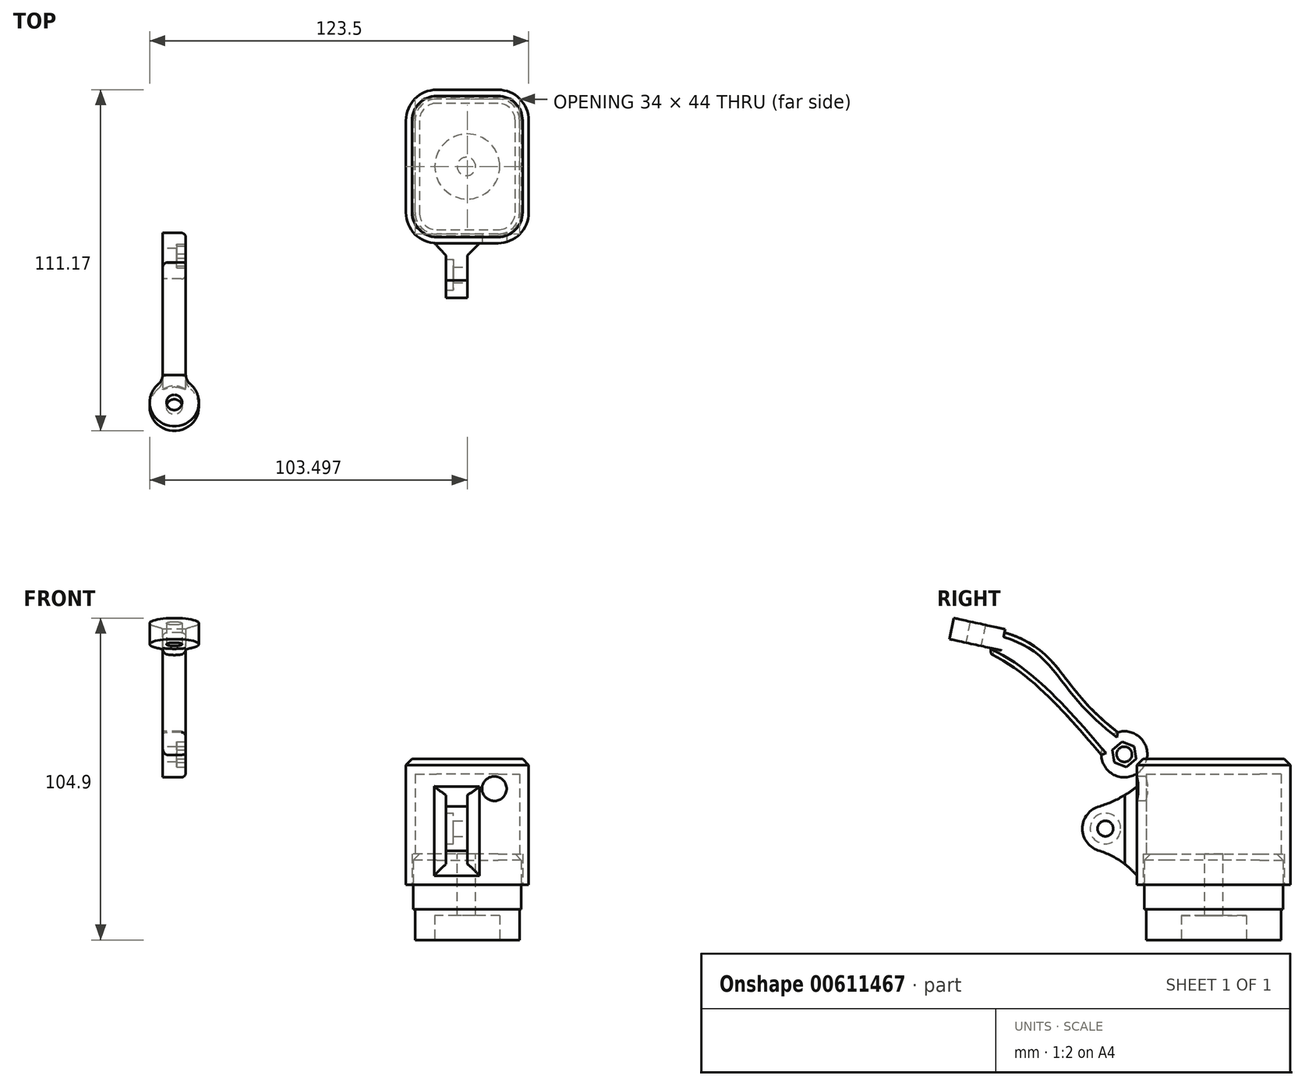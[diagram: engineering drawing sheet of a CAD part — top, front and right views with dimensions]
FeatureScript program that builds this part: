
annotation { "Feature Type Name" : "Feature", "Feature Type Description" : "" }
export const myFeature = defineFeature(function(context is Context, id is Id, definition is map)
    precondition{}
    {
        {
            var Q0;
            Q0=qCreatedBy(makeId("Right.planeOp"),FACE);
            var sketch = newSketch(context, id + "F0", { "sketchPlane" : qUnion([Q0])});
            skCircle(sketch, "E0", {"center": v(-29.14, 42.5) * mm, "radius": 3.6 * mm});
            skCircle(sketch, "E1", {"center": v(-29.14, 42.5) * mm, "radius": 5 * mm});
            skLineSegment(sketch, "E2", {"start": v(-69.14, 82.5) * mm, "end": v(-82.83, 85.47) * mm});
            skCircle(sketch, "E3", {"center": v(-29.14, 42.5) * mm, "radius": 7.5 * mm});
            skFitSpline(sketch, "E4", {"points": [v(-11.21, 52.43) * mm, v(-17.95, 9.37) * mm], "startDerivative": vector(-15.47, -15.75) * mm, "endDerivative": vector(-1.67, -37.36) * mm});
            skFitSpline(sketch, "E5", {"points": [v(-22.8, 46.5) * mm, v(-11.21, 52.43) * mm], "startDerivative": vector(15.63, -7.91) * mm, "endDerivative": vector(13.09, 9.04) * mm});
            skFitSpline(sketch, "E6", {"points": [v(-32.57, 35.83) * mm, v(-17.95, 9.37) * mm], "startDerivative": vector(25.66, -14.01) * mm, "endDerivative": vector(10.19, -17.27) * mm});
            skLineSegment(sketch, "E7", {"start": v(-16.89, 47.19) * mm, "end": v(-26.36, 29.28) * mm});
            skLineSegment(sketch, "E8.0", {"start": v(-69.4, 76.41) * mm, "end": v(-84.58, 79.7) * mm});
            skLineSegment(sketch, "E9", {"start": v(-69.4, 76.41) * mm, "end": v(-69.14, 82.5) * mm});
            skLineSegment(sketch, "E10", {"start": v(-84.58, 79.7) * mm, "end": v(-82.83, 85.47) * mm});
            skCircle(sketch, "E11", {"center": v(-29.14, 42.5) * mm, "radius": 6.25 * mm});
            skFitSpline(sketch, "E12", {"points": [v(-35.04, 40.42) * mm, v(-84.58, 79.7) * mm], "startDerivative": vector(-65.8, 78.38) * mm, "endDerivative": vector(-54.37, 15.9) * mm});
            skFitSpline(sketch, "E13", {"points": [v(-28.15, 47.4) * mm, v(-69.14, 82.5) * mm], "startDerivative": vector(-71.86, 50.82) * mm, "endDerivative": vector(-64.05, 18.36) * mm});
            skCircle(sketch, "E14.cCircle", {"center": v(-29.14, 42.5) * mm, "radius": 3.6 * mm, "construction": true});
            skLineSegment(sketch, "E14.0", {"start": v(-33.03, 43.97) * mm, "end": v(-29.82, 46.6) * mm});
            skLineSegment(sketch, "E14.1", {"start": v(-29.82, 46.6) * mm, "end": v(-25.93, 45.13) * mm});
            skLineSegment(sketch, "E14.2", {"start": v(-25.93, 45.13) * mm, "end": v(-25.26, 41.03) * mm});
            skLineSegment(sketch, "E14.3", {"start": v(-25.26, 41.03) * mm, "end": v(-28.47, 38.4) * mm});
            skLineSegment(sketch, "E14.4", {"start": v(-28.47, 38.4) * mm, "end": v(-32.36, 39.87) * mm});
            skLineSegment(sketch, "E14.5", {"start": v(-32.36, 39.87) * mm, "end": v(-33.03, 43.97) * mm});
            skPoint(sketch, "E14.0.midPoint", {"position": v(-31.42, 45.28) * mm});
            skSolve(sketch);
        }
        {
            var Q0;
            {var subQ1=sQuery(id+"F0.wireOp",EDGE,"E8.0");Q0=makeQuery(id+"F0.imprint","IMPRINT",FACE,{"disambiguationData":[TD([[makeQuery(id+"F0.imprint","IMPRINT",EDGE,{"derivedFrom":subQ1}),1.0]])]});}
            var Q1;
            {var subQ0=sQuery(id+"F0.wireOp",EDGE,"E13");var subQ1=sQuery(id+"F0.wireOp",EDGE,"E3");var subQ2=makeQuery(id+"F0.imprint","INTERSECT",VERTEX,{"derivedFrom":[subQ1,subQ0]});Q1=makeQuery(id+"F0.imprint","IMPRINT",FACE,{"disambiguationData":[TD([[makeQuery(id+"F0.imprint","IMPRINT",EDGE,{"disambiguationData":[TD([[subQ2,-1.0]])],"derivedFrom":subQ1}),1.0]])]});}
            var Q2;
            Q2=makeQuery(id+"F0.imprint","IMPRINT",FACE,{"disambiguationData":[TD([[makeQuery(id+"F0.imprint","IMPRINT",EDGE,{"derivedFrom":sQuery(id+"F0.wireOp",EDGE,"E1")}),-1.0]])]});
            var Q3;
            Q3=makeQuery(id+"F0.imprint","IMPRINT",FACE,{"disambiguationData":[TD([[makeQuery(id+"F0.imprint","IMPRINT",EDGE,{"derivedFrom":sQuery(id+"F0.wireOp",EDGE,"E0")}),-1.0]])]});
            var Q4;
            Q4=makeQuery(id+"F0.imprint","IMPRINT",FACE,{"disambiguationData":[TD([[makeQuery(id+"F0.imprint","IMPRINT",EDGE,{"derivedFrom":sQuery(id+"F0.wireOp",EDGE,"E0")}),1.0]])]});
            var Q5;
            Q5=makeQuery(id+"F0.imprint","IMPRINT",FACE,{"disambiguationData":[TD([[makeQuery(id+"F0.imprint","IMPRINT",EDGE,{"derivedFrom":sQuery(id+"F0.wireOp",EDGE,"E1")}),1.0]])]});
            var Q6;
            {var subQ1=sQuery(id+"F0.wireOp",EDGE,"E3");var subQ4=makeQuery(id+"F0.imprint","INTERSECT",VERTEX,{"derivedFrom":[subQ1,sQuery(id+"F0.wireOp",EDGE,"E5")]});Q6=makeQuery(id+"F0.imprint","IMPRINT",FACE,{"disambiguationData":[TD([[makeQuery(id+"F0.imprint","IMPRINT",EDGE,{"disambiguationData":[TD([[subQ4,-1.0]])],"derivedFrom":subQ1}),1.0]])]});}
            extrude(context, id + "F1", {"entities" : qUnion([Q0, Q1, Q2, Q3, Q4, Q5, Q6]), "depth" : 7.5 * mm, "offsetDistance" : 25 * mm});
        }
        {
            var Q0;
            Q0=makeQuery(id+"F1.opExtrude","CAP_FACE",FACE,{"disambiguationData":[OSD([sQuery(id+"F0.wireOp",EDGE,"E8.0"),sQuery(id+"F0.wireOp",EDGE,"E9"),sQuery(id+"F0.wireOp",EDGE,"E11"),sQuery(id+"F0.wireOp",EDGE,"E12"),sQuery(id+"F0.wireOp",EDGE,"E13")])],"isStart":false});
            var sketch = newSketch(context, id + "F2", { "sketchPlane" : qUnion([Q0])});
            skLineSegment(sketch, "E15.0", {"start": v(-32.36, 39.87) * mm, "end": v(-33.03, 43.97) * mm});
            skLineSegment(sketch, "E15.1", {"start": v(-28.47, 38.4) * mm, "end": v(-32.36, 39.87) * mm});
            skLineSegment(sketch, "E15.2", {"start": v(-25.26, 41.03) * mm, "end": v(-28.47, 38.4) * mm});
            skLineSegment(sketch, "E15.3", {"start": v(-25.93, 45.13) * mm, "end": v(-25.26, 41.03) * mm});
            skLineSegment(sketch, "E15.4", {"start": v(-29.82, 46.6) * mm, "end": v(-25.93, 45.13) * mm});
            skLineSegment(sketch, "E15.5", {"start": v(-33.03, 43.97) * mm, "end": v(-29.82, 46.6) * mm});
            skSolve(sketch);
        }
        {
            var Q0;
            Q0=makeQuery(id+"F2.imprint","IMPRINT",FACE,{"disambiguationData":[TD([[makeQuery(id+"F2.imprint","IMPRINT",EDGE,{"derivedFrom":sQuery(id+"F2.wireOp",EDGE,"E15.0")}),-1.0]])]});
            extrude(context, id + "F3", {"entities" : qUnion([Q0]), "operationType" : NewBodyOperationType.REMOVE, "oppositeDirection" : true, "depth" : 3 * mm});
        }
        {
            var Q0;
            Q0=sQuery(id+"F0.wireOp",VERTEX,"E0.center");
            var Q1;
            Q1=makeQuery(id+"F1.opExtrude","SWEPT_BODY",BODY,{"disambiguationData":[OSD([sQuery(id+"F0.wireOp",EDGE,"E3"),sQuery(id+"F0.wireOp",EDGE,"E6"),sQuery(id+"F0.wireOp",EDGE,"E8.0"),sQuery(id+"F0.wireOp",EDGE,"E9"),sQuery(id+"F0.wireOp",EDGE,"E12"),sQuery(id+"F0.wireOp",EDGE,"E13")])]});
            hole(context, id + "F4", {"style" : HoleStyle.SIMPLE, "endStyle" : HoleEndStyle.THROUGH, "oppositeDirection" : true, "holeDiameter" : 5 * mm, "isTappedThrough" : true, "tappedDepth" : 12 * mm, "tapClearance" : 3, "locations" : qUnion([Q0]), "scope" : qUnion([Q1]), "majorDiameter" : 5 * mm});
        }
        {
            var Q0;
            Q0=makeQuery(id+"F1.opExtrude","CAP_EDGE",EDGE,{"disambiguationData":[OSD([sQuery(id+"F0.wireOp",EDGE,"E12")])],"isStart":false});
            var Q1;
            Q1=makeQuery(id+"F1.opExtrude","CAP_EDGE",EDGE,{"disambiguationData":[OSD([sQuery(id+"F0.wireOp",EDGE,"E13")])],"isStart":false});
            var Q2;
            Q2=makeQuery(id+"F1.opExtrude","CAP_EDGE",EDGE,{"disambiguationData":[OSD([sQuery(id+"F0.wireOp",EDGE,"E12")])],"isStart":true});
            var Q3;
            Q3=makeQuery(id+"F1.opExtrude","CAP_EDGE",EDGE,{"disambiguationData":[OSD([sQuery(id+"F0.wireOp",EDGE,"E13")])],"isStart":true});
            var Q4;
            {var subQ0=sQuery(id+"F0.wireOp",EDGE,"E3");var subQ1=makeQuery(id+"F0.imprint","INTERSECT",VERTEX,{"derivedFrom":[subQ0,sQuery(id+"F0.wireOp",EDGE,"E5")]});Q4=makeQuery(id+"F1.opExtrude","CAP_EDGE",EDGE,{"disambiguationData":[OSD([subQ0]),TDD([makeQuery(id+"F0.imprint","IMPRINT",EDGE,{"disambiguationData":[TD([[subQ1,-1.0]])],"derivedFrom":subQ0}),makeQuery(id+"F0.imprint","IMPRINT",EDGE,{"disambiguationData":[TD([[subQ1,1.0]])],"derivedFrom":subQ0})])],"isStart":false});}
            var Q5;
            Q5=makeQuery(id+"F1.opExtrude","CAP_EDGE",EDGE,{"disambiguationData":[OSD([sQuery(id+"F0.wireOp",EDGE,"E6")])],"isStart":false});
            var Q6;
            {var subQ0=sQuery(id+"F0.wireOp",EDGE,"E3");Q6=makeQuery(id+"F1.opExtrude","CAP_EDGE",EDGE,{"disambiguationData":[OSD([subQ0]),TDD([makeQuery(id+"F0.imprint","IMPRINT",EDGE,{"disambiguationData":[TD([[makeQuery(id+"F0.imprint","INTERSECT",VERTEX,{"disambiguationData":[OD(0.0)],"derivedFrom":[subQ0,sQuery(id+"F0.wireOp",EDGE,"E6")]}),1.0]])],"derivedFrom":subQ0})])],"isStart":false});}
            fillet(context, id + "F5", {"entities" : qUnion([Q0, Q1, Q2, Q3, Q4, Q5, Q6]), "radius" : 1.5 * mm, "tangentPropagation" : true, "allowEdgeOverflow" : false});
        }
        {
            var Q0;
            Q0=makeQuery(id+"F1.opExtrude","SWEPT_FACE",FACE,{"disambiguationData":[OSD([sQuery(id+"F0.wireOp",EDGE,"E8.0")])]});
            var sketch = newSketch(context, id + "F6", { "sketchPlane" : qUnion([Q0])});
            skCircle(sketch, "E16", {"center": v(3.75, -93.2) * mm, "radius": 8 * mm});
            skPoint(sketch, "E16.centerSnap0", {"position": v(3.75, -99.56) * mm});
            skSolve(sketch);
        }
        {
            var Q0;
            {var subQ0=sQuery(id+"F0.wireOp",EDGE,"E8.0");var subQ1=makeQuery(id+"F1.opExtrude","SWEPT_FACE",FACE,{"disambiguationData":[OSD([subQ0])]});var subQ2=sQuery(id+"F0.wireOp",EDGE,"E12");var subQ4=makeQuery(id+"F5.opFillet","BLEND_EDGE",EDGE,{"blendedFrom":[makeQuery(id+"F1.opExtrude","CAP_EDGE",EDGE,{"disambiguationData":[OSD([subQ2])],"isStart":true}),subQ1],"blendedInto":[subQ1]});Q0=makeQuery(id+"F6.imprint","IMPRINT",FACE,{"disambiguationData":[TD([[makeQuery(id+"F6.imprint","IMPRINT",EDGE,{"derivedFrom":subQ4}),-1.0]])]});}
            var Q1;
            {var subQ0=sQuery(id+"F0.wireOp",EDGE,"E8.0");var subQ1=makeQuery(id+"F1.opExtrude","SWEPT_FACE",FACE,{"disambiguationData":[OSD([subQ0])]});var subQ2=sQuery(id+"F0.wireOp",EDGE,"E12");var subQ3=makeQuery(id+"F5.opFillet","BLEND_EDGE",EDGE,{"blendedFrom":[makeQuery(id+"F1.opExtrude","CAP_EDGE",EDGE,{"disambiguationData":[OSD([subQ2])],"isStart":true}),subQ1],"blendedInto":[subQ1]});Q1=makeQuery(id+"F6.imprint","IMPRINT",FACE,{"disambiguationData":[TD([[makeQuery(id+"F6.imprint","IMPRINT",EDGE,{"derivedFrom":subQ3}),1.0]])]});}
            var Q2;
            {var subQ1=sQuery(id+"F0.wireOp",EDGE,"E8.0");var subQ6=makeQuery(id+"F1.opExtrude","SWEPT_EDGE",EDGE,{"disambiguationData":[OSD([subQ1,sQuery(id+"F0.wireOp",EDGE,"E9")])]});Q2=makeQuery(id+"F6.imprint","IMPRINT",FACE,{"disambiguationData":[TD([[makeQuery(id+"F6.imprint","IMPRINT",EDGE,{"derivedFrom":subQ6}),1.0]])]});}
            extrude(context, id + "F7", {"entities" : qUnion([Q0, Q1, Q2]), "operationType" : NewBodyOperationType.ADD, "depth" : 7 * mm, "offsetDistance" : 25 * mm});
        }
        {
            var Q0;
            Q0=sQuery(id+"F6.wireOp",VERTEX,"E16.center");
            var Q1;
            Q1=makeQuery(id+"F1.opExtrude","SWEPT_BODY",BODY,{"disambiguationData":[OSD([sQuery(id+"F0.wireOp",EDGE,"E3"),sQuery(id+"F0.wireOp",EDGE,"E6"),sQuery(id+"F0.wireOp",EDGE,"E8.0"),sQuery(id+"F0.wireOp",EDGE,"E9"),sQuery(id+"F0.wireOp",EDGE,"E12"),sQuery(id+"F0.wireOp",EDGE,"E13")])]});
            hole(context, id + "F8", {"style" : HoleStyle.SIMPLE, "endStyle" : HoleEndStyle.THROUGH, "oppositeDirection" : true, "holeDiameter" : 5.1 * mm, "isTappedThrough" : true, "tappedDepth" : 12 * mm, "tapClearance" : 3, "locations" : qUnion([Q0]), "scope" : qUnion([Q1]), "majorDiameter" : 5 * mm});
        }
        {
            var Q0;
            Q0=sQuery(id+"F6.wireOp",VERTEX,"E16.center");
            var Q1;
            Q1=makeQuery(id+"F1.opExtrude","SWEPT_BODY",BODY,{"disambiguationData":[OSD([sQuery(id+"F0.wireOp",EDGE,"E3"),sQuery(id+"F0.wireOp",EDGE,"E6"),sQuery(id+"F0.wireOp",EDGE,"E8.0"),sQuery(id+"F0.wireOp",EDGE,"E9"),sQuery(id+"F0.wireOp",EDGE,"E12"),sQuery(id+"F0.wireOp",EDGE,"E13")])]});
            hole(context, id + "F9", {"style" : HoleStyle.C_BORE, "endStyle" : HoleEndStyle.THROUGH, "holeDiameter" : 5 * mm, "cBoreDiameter" : 14 * mm, "cBoreDepth" : 4 * mm, "isTappedThrough" : true, "tappedDepth" : 12 * mm, "tapClearance" : 3, "locations" : qUnion([Q0]), "scope" : qUnion([Q1]), "majorDiameter" : 5 * mm});
        }
        {
            var Q0;
            {var subQ0=sQuery(id+"F6.wireOp",EDGE,"E16");var subQ1=sQuery(id+"F0.wireOp",EDGE,"E8.0");Q0=makeQuery(id+"F7.opExtrude","SWEPT_EDGE",EDGE,{"disambiguationData":[OSD([subQ1,subQ0]),TDD([makeQuery(id+"F6.imprint","INTERSECT",VERTEX,{"derivedFrom":[makeQuery(id+"F1.opExtrude","CAP_EDGE",EDGE,{"disambiguationData":[OSD([subQ1])],"isStart":false}),subQ0]})])]});}
            var Q1;
            {var subQ0=sQuery(id+"F6.wireOp",EDGE,"E16");var subQ1=sQuery(id+"F0.wireOp",EDGE,"E8.0");Q1=makeQuery(id+"F7.opExtrude","SWEPT_EDGE",EDGE,{"disambiguationData":[OSD([subQ1,subQ0]),TDD([makeQuery(id+"F6.imprint","INTERSECT",VERTEX,{"derivedFrom":[makeQuery(id+"F1.opExtrude","CAP_EDGE",EDGE,{"disambiguationData":[OSD([subQ1])],"isStart":true}),subQ0]})])]});}
            fillet(context, id + "F10", {"entities" : qUnion([Q0, Q1]), "radius" : 4.6 * mm, "tangentPropagation" : true, "allowEdgeOverflow" : false});
        }
        {
            var Q0;
            Q0=qCreatedBy(makeId("Top.planeOp"),FACE);
            var sketch = newSketch(context, id + "F11", { "sketchPlane" : qUnion([Q0])});
            skLineSegment(sketch, "E17.bottom", {"start": v(109.25, -25) * mm, "end": v(89.25, -25) * mm});
            skLineSegment(sketch, "E17.top", {"start": v(109.25, 25) * mm, "end": v(89.25, 25) * mm});
            skLineSegment(sketch, "E17.left", {"start": v(119.25, -15) * mm, "end": v(119.25, 15) * mm});
            skLineSegment(sketch, "E17.right", {"start": v(79.25, -15) * mm, "end": v(79.25, 15) * mm});
            skPoint(sketch, "E17.middle", {"position": v(99.25, 0) * mm});
            skPoint(sketch, "E18.visualSharp", {"position": v(79.25, -25) * mm});
            skArc(sketch, "E18.filletArc", {"start": v(79.25, -15) * mm, "mid": v(82.18, -22.07) * mm, "end": v(89.25, -25) * mm});
            skPoint(sketch, "E19.visualSharp", {"position": v(119.25, -25) * mm});
            skArc(sketch, "E19.filletArc", {"start": v(109.25, -25) * mm, "mid": v(116.32, -22.07) * mm, "end": v(119.25, -15) * mm});
            skPoint(sketch, "E20.visualSharp", {"position": v(119.25, 25) * mm});
            skArc(sketch, "E20.filletArc", {"start": v(119.25, 15) * mm, "mid": v(116.32, 22.07) * mm, "end": v(109.25, 25) * mm});
            skPoint(sketch, "E21.visualSharp", {"position": v(79.25, 25) * mm});
            skArc(sketch, "E21.filletArc", {"start": v(89.25, 25) * mm, "mid": v(82.18, 22.07) * mm, "end": v(79.25, 15) * mm});
            skLineSegment(sketch, "E22.0", {"start": v(117.25, -15) * mm, "end": v(117.25, 15) * mm});
            skArc(sketch, "E22.1", {"start": v(109.25, -23) * mm, "mid": v(114.9, -20.66) * mm, "end": v(117.25, -15) * mm});
            skArc(sketch, "E22.2", {"start": v(117.25, 15) * mm, "mid": v(114.9, 20.66) * mm, "end": v(109.25, 23) * mm});
            skLineSegment(sketch, "E22.3", {"start": v(109.25, -23) * mm, "end": v(89.25, -23) * mm});
            skLineSegment(sketch, "E22.4", {"start": v(109.25, 23) * mm, "end": v(89.25, 23) * mm});
            skArc(sketch, "E22.5", {"start": v(89.25, 23) * mm, "mid": v(83.6, 20.66) * mm, "end": v(81.25, 15) * mm});
            skLineSegment(sketch, "E22.6", {"start": v(81.25, -15) * mm, "end": v(81.25, 15) * mm});
            skArc(sketch, "E22.7", {"start": v(81.25, -15) * mm, "mid": v(83.6, -20.66) * mm, "end": v(89.25, -23) * mm});
            skLineSegment(sketch, "E23", {"start": v(99.25, 34.03) * mm, "end": v(99.25, -73.15) * mm, "construction": true});
            skPoint(sketch, "E23.endSnap0", {"position": v(99.25, -25) * mm});
            skPoint(sketch, "E24.visualSharp", {"position": v(111.25, 7) * mm});
            skPoint(sketch, "E25.visualSharp", {"position": v(87.25, 7) * mm});
            skPoint(sketch, "E26.visualSharp", {"position": v(87.25, -7) * mm});
            skPoint(sketch, "E27.visualSharp", {"position": v(111.25, -7) * mm});
            skArc(sketch, "E28.0", {"start": v(109.25, -22) * mm, "mid": v(114.2, -19.95) * mm, "end": v(116.25, -15) * mm});
            skLineSegment(sketch, "E28.1", {"start": v(109.25, -22) * mm, "end": v(89.25, -22) * mm});
            skLineSegment(sketch, "E28.2", {"start": v(116.25, -15) * mm, "end": v(116.25, 15) * mm});
            skArc(sketch, "E28.3", {"start": v(82.25, -15) * mm, "mid": v(84.3, -19.95) * mm, "end": v(89.25, -22) * mm});
            skArc(sketch, "E28.4", {"start": v(116.25, 15) * mm, "mid": v(114.2, 19.95) * mm, "end": v(109.25, 22) * mm});
            skLineSegment(sketch, "E28.5", {"start": v(109.25, 22) * mm, "end": v(89.25, 22) * mm});
            skArc(sketch, "E28.6", {"start": v(89.25, 22) * mm, "mid": v(84.3, 19.95) * mm, "end": v(82.25, 15) * mm});
            skLineSegment(sketch, "E28.7", {"start": v(82.25, -15) * mm, "end": v(82.25, 15) * mm});
            skSolve(sketch);
        }
        {
            var Q0;
            Q0=qSketchRegion(id+"F11",true);
            var Q1;
            Q1=makeQuery(id+"F11.imprint","IMPRINT",FACE,{"disambiguationData":[TD([[makeQuery(id+"F11.imprint","IMPRINT",EDGE,{"derivedFrom":sQuery(id+"F11.wireOp",EDGE,"E22.0")}),1.0]])]});
            extrude(context, id + "F12", {"entities" : qUnion([Q0, Q1]), "depth" : 36 * mm, "offsetDistance" : 25.4 * mm});
        }
        {
            var Q0;
            Q0=makeQuery(id+"F11.imprint","IMPRINT",FACE,{"disambiguationData":[TD([[makeQuery(id+"F11.imprint","IMPRINT",EDGE,{"derivedFrom":sQuery(id+"F11.wireOp",EDGE,"E22.0")}),1.0]])]});
            var Q1;
            Q1=makeQuery(id+"F11.imprint","IMPRINT",FACE,{"disambiguationData":[TD([[makeQuery(id+"F11.imprint","IMPRINT",EDGE,{"derivedFrom":sQuery(id+"F11.wireOp",EDGE,"E17.bottom")}),-1.0]])]});
            var Q2;
            Q2=makeQuery(id+"F11.imprint","IMPRINT",FACE,{"disambiguationData":[TD([[makeQuery(id+"F11.imprint","IMPRINT",EDGE,{"derivedFrom":sQuery(id+"F11.wireOp",EDGE,"Csc6OuQQ-H8ih-5Qqx-3U0u-JoZDeYAVxKeH")}),-1.0]])]});
            var Q3;
            Q3=makeQuery(id+"F11.imprint","IMPRINT",FACE,{"disambiguationData":[TD([[makeQuery(id+"F11.imprint","IMPRINT",EDGE,{"derivedFrom":sQuery(id+"F11.wireOp",EDGE,"Csc6OuQQ-H8ih-5Qqx-3U0u-JoZDeYAVxKeH")}),1.0]])]});
            var Q4;
            Q4=makeQuery(id+"F11.imprint","IMPRINT",FACE,{"disambiguationData":[TD([[makeQuery(id+"F11.imprint","IMPRINT",EDGE,{"derivedFrom":sQuery(id+"F11.wireOp",EDGE,"90596eee-9654-42a0-ac1d-bc8a5213f9b5.1")}),1.0]])]});
            var Q5;
            Q5=makeQuery(id+"F11.imprint","IMPRINT",FACE,{"disambiguationData":[TD([[makeQuery(id+"F11.imprint","IMPRINT",EDGE,{"derivedFrom":sQuery(id+"F11.wireOp",EDGE,"E28.0")}),1.0]])]});
            extrude(context, id + "F13", {"entities" : qUnion([Q0, Q1, Q2, Q3, Q4, Q5]), "depth" : 41 * mm, "offsetDistance" : 77 * mm, "hasSecondDirection" : true, "secondDirectionOppositeDirection" : false, "secondDirectionDepth" : 36 * mm});
        }
        {
            var Q0;
            Q0=qCreatedBy(makeId("Right.planeOp"),FACE);
            var Q1;
            Q1=sQuery(id+"F11.wireOp",VERTEX,"E17.middle");
            cPlane(context, id + "F14", {"entities" : qUnion([Q0, Q1]), "cplaneType" : CPlaneType.PLANE_POINT, "offset" : 25 * mm, "width" : 150 * mm, "height" : 150 * mm});
        }
        {
            var Q0;
            Q0=qCreatedBy(id+"F14.planeOp",FACE);
            var sketch = newSketch(context, id + "F15", { "sketchPlane" : qUnion([Q0])});
            skCircle(sketch, "E29", {"center": v(-35.31, 18.3) * mm, "radius": 3.6 * mm});
            skCircle(sketch, "E30", {"center": v(-35.31, 18.3) * mm, "radius": 5 * mm});
            skCircle(sketch, "E31", {"center": v(-35.31, 18.3) * mm, "radius": 7.5 * mm});
            skCircle(sketch, "E32", {"center": v(-35.31, 18.3) * mm, "radius": 6.25 * mm});
            skCircle(sketch, "E33.cCircle", {"center": v(-35.31, 18.3) * mm, "radius": 3.6 * mm, "construction": true});
            skLineSegment(sketch, "E33.0", {"start": v(-39.44, 17.83) * mm, "end": v(-37.79, 21.64) * mm});
            skLineSegment(sketch, "E33.1", {"start": v(-37.79, 21.64) * mm, "end": v(-33.66, 22.12) * mm});
            skLineSegment(sketch, "E33.2", {"start": v(-33.66, 22.12) * mm, "end": v(-31.18, 18.78) * mm});
            skLineSegment(sketch, "E33.3", {"start": v(-31.18, 18.78) * mm, "end": v(-32.84, 14.96) * mm});
            skLineSegment(sketch, "E33.4", {"start": v(-32.84, 14.96) * mm, "end": v(-36.97, 14.5) * mm});
            skLineSegment(sketch, "E33.5", {"start": v(-36.97, 14.5) * mm, "end": v(-39.44, 17.83) * mm});
            skPoint(sketch, "E33.0.midPoint", {"position": v(-38.61, 19.74) * mm});
            skLineSegment(sketch, "E34.0", {"start": v(-70.88, 0) * mm, "end": v(-35.31, 18.3) * mm, "construction": true});
            skLineSegment(sketch, "E35", {"start": v(-24.37, 32.56) * mm, "end": v(-24.37, 2.16) * mm});
            skArc(sketch, "E36", {"start": v(-24.37, 2.16) * mm, "mid": v(-30.08, 7.52) * mm, "end": v(-37.08, 11.02) * mm});
            skArc(sketch, "E37", {"start": v(-37.7, 25.41) * mm, "mid": v(-30.65, 28.27) * mm, "end": v(-24.37, 32.56) * mm});
            skArc(sketch, "E38", {"start": v(-24.37, 32.56) * mm, "mid": v(-27.66, 17.36) * mm, "end": v(-24.37, 2.16) * mm});
            skSolve(sketch);
        }
        {
            var Q0;
            Q0=makeQuery(id+"F15.imprint","IMPRINT",FACE,{"disambiguationData":[TD([[makeQuery(id+"F15.imprint","IMPRINT",EDGE,{"derivedFrom":sQuery(id+"F15.wireOp",EDGE,"E35")}),-1.0]])]});
            var Q1;
            {var subQ5=sQuery(id+"F15.wireOp",EDGE,"E31");var subQ7=makeQuery(id+"F15.imprint","INTERSECT",VERTEX,{"derivedFrom":[subQ5,sQuery(id+"F15.wireOp",EDGE,"E37")]});Q1=makeQuery(id+"F15.imprint","IMPRINT",FACE,{"disambiguationData":[TD([[makeQuery(id+"F15.imprint","IMPRINT",EDGE,{"disambiguationData":[TD([[subQ7,-1.0]])],"derivedFrom":subQ5}),1.0]])]});}
            var Q2;
            {var subQ0=sQuery(id+"F15.wireOp",EDGE,"8196ae58-aa4e-4321-9e98-37394b98831b");var subQ1=sQuery(id+"F15.wireOp",EDGE,"E31");var subQ2=makeQuery(id+"F15.imprint","INTERSECT",VERTEX,{"derivedFrom":[subQ1,subQ0]});Q2=makeQuery(id+"F15.imprint","IMPRINT",FACE,{"disambiguationData":[TD([[makeQuery(id+"F15.imprint","IMPRINT",EDGE,{"disambiguationData":[TD([[subQ2,-1.0]])],"derivedFrom":subQ1}),1.0]])]});}
            var Q3;
            Q3=makeQuery(id+"F15.imprint","IMPRINT",FACE,{"disambiguationData":[TD([[makeQuery(id+"F15.imprint","IMPRINT",EDGE,{"derivedFrom":sQuery(id+"F15.wireOp",EDGE,"E30")}),-1.0]])]});
            var Q4;
            {var subQ0=sQuery(id+"F15.wireOp",EDGE,"E37");var subQ1=sQuery(id+"F15.wireOp",EDGE,"E31");var subQ2=makeQuery(id+"F15.imprint","INTERSECT",VERTEX,{"derivedFrom":[subQ1,subQ0]});Q4=makeQuery(id+"F15.imprint","IMPRINT",FACE,{"disambiguationData":[TD([[makeQuery(id+"F15.imprint","IMPRINT",EDGE,{"disambiguationData":[TD([[subQ2,1.0]])],"derivedFrom":subQ1}),-1.0]])]});}
            var Q5;
            {var subQ0=sQuery(id+"F15.wireOp",EDGE,"E36");var subQ1=sQuery(id+"F15.wireOp",EDGE,"E31");var subQ2=makeQuery(id+"F15.imprint","INTERSECT",VERTEX,{"derivedFrom":[subQ1,subQ0]});Q5=makeQuery(id+"F15.imprint","IMPRINT",FACE,{"disambiguationData":[TD([[makeQuery(id+"F15.imprint","IMPRINT",EDGE,{"disambiguationData":[TD([[subQ2,-1.0]])],"derivedFrom":subQ1}),-1.0]])]});}
            extrude(context, id + "F16", {"entities" : qUnion([Q0, Q1, Q2, Q3, Q4, Q5]), "operationType" : NewBodyOperationType.ADD, "oppositeDirection" : true, "depth" : 7 * mm, "offsetDistance" : 25 * mm});
        }
        {
            var Q0;
            {var subQ0=sQuery(id+"F15.wireOp",EDGE,"E33.1");var subQ1=sQuery(id+"F15.wireOp",EDGE,"E29");var subQ2=makeQuery(id+"F15.imprint","INTERSECT",VERTEX,{"derivedFrom":[subQ1,subQ0]});Q0=makeQuery(id+"F15.imprint","IMPRINT",FACE,{"disambiguationData":[TD([[makeQuery(id+"F15.imprint","IMPRINT",EDGE,{"disambiguationData":[TD([[subQ2,1.0]])],"derivedFrom":subQ1}),-1.0]])]});}
            var Q1;
            {var subQ0=sQuery(id+"F15.wireOp",EDGE,"E33.2");var subQ1=sQuery(id+"F15.wireOp",EDGE,"E29");var subQ2=makeQuery(id+"F15.imprint","INTERSECT",VERTEX,{"derivedFrom":[subQ1,subQ0]});Q1=makeQuery(id+"F15.imprint","IMPRINT",FACE,{"disambiguationData":[TD([[makeQuery(id+"F15.imprint","IMPRINT",EDGE,{"disambiguationData":[TD([[subQ2,1.0]])],"derivedFrom":subQ1}),-1.0]])]});}
            var Q2;
            {var subQ0=sQuery(id+"F15.wireOp",EDGE,"E33.4");var subQ1=sQuery(id+"F15.wireOp",EDGE,"E29");var subQ2=makeQuery(id+"F15.imprint","INTERSECT",VERTEX,{"derivedFrom":[subQ1,subQ0]});Q2=makeQuery(id+"F15.imprint","IMPRINT",FACE,{"disambiguationData":[TD([[makeQuery(id+"F15.imprint","IMPRINT",EDGE,{"disambiguationData":[TD([[subQ2,-1.0]])],"derivedFrom":subQ1}),-1.0]])]});}
            var Q3;
            {var subQ0=sQuery(id+"F15.wireOp",EDGE,"E33.5");var subQ1=sQuery(id+"F15.wireOp",EDGE,"E29");var subQ2=makeQuery(id+"F15.imprint","INTERSECT",VERTEX,{"derivedFrom":[subQ1,subQ0]});Q3=makeQuery(id+"F15.imprint","IMPRINT",FACE,{"disambiguationData":[TD([[makeQuery(id+"F15.imprint","IMPRINT",EDGE,{"disambiguationData":[TD([[subQ2,-1.0]])],"derivedFrom":subQ1}),-1.0]])]});}
            var Q4;
            {var subQ0=sQuery(id+"F15.wireOp",EDGE,"E33.0");var subQ1=sQuery(id+"F15.wireOp",EDGE,"E29");var subQ2=makeQuery(id+"F15.imprint","INTERSECT",VERTEX,{"derivedFrom":[subQ1,subQ0]});Q4=makeQuery(id+"F15.imprint","IMPRINT",FACE,{"disambiguationData":[TD([[makeQuery(id+"F15.imprint","IMPRINT",EDGE,{"disambiguationData":[TD([[subQ2,-1.0]])],"derivedFrom":subQ1}),-1.0]])]});}
            var Q5;
            {var subQ0=sQuery(id+"F15.wireOp",EDGE,"E33.1");var subQ1=sQuery(id+"F15.wireOp",EDGE,"E29");var subQ2=makeQuery(id+"F15.imprint","INTERSECT",VERTEX,{"derivedFrom":[subQ1,subQ0]});Q5=makeQuery(id+"F15.imprint","IMPRINT",FACE,{"disambiguationData":[TD([[makeQuery(id+"F15.imprint","IMPRINT",EDGE,{"disambiguationData":[TD([[subQ2,-1.0]])],"derivedFrom":subQ1}),-1.0]])]});}
            var Q6;
            Q6=makeQuery(id+"F15.imprint","IMPRINT",FACE,{"disambiguationData":[TD([[makeQuery(id+"F15.imprint","IMPRINT",EDGE,{"derivedFrom":sQuery(id+"F15.wireOp",EDGE,"E30")}),1.0]])]});
            var Q7;
            {var subQ0=sQuery(id+"F15.wireOp",EDGE,"E29");var subQ4=makeQuery(id+"F15.imprint","INTERSECT",VERTEX,{"derivedFrom":[subQ0,sQuery(id+"F15.wireOp",EDGE,"E33.1")]});Q7=makeQuery(id+"F15.imprint","IMPRINT",FACE,{"disambiguationData":[TD([[makeQuery(id+"F15.imprint","IMPRINT",EDGE,{"disambiguationData":[TD([[subQ4,1.0]])],"derivedFrom":subQ0}),1.0]])]});}
            extrude(context, id + "F17", {"entities" : qUnion([Q0, Q1, Q2, Q3, Q4, Q5, Q6, Q7]), "operationType" : NewBodyOperationType.ADD, "oppositeDirection" : true, "depth" : 4.5 * mm, "offsetDistance" : 25 * mm});
        }
        {
            var Q0;
            Q0=sQuery(id+"F15.wireOp",VERTEX,"E34.0.end");
            var Q1;
            Q1=makeQuery(id+"F12.opExtrude","SWEPT_BODY",BODY,{"disambiguationData":[OSD([sQuery(id+"F11.wireOp",EDGE,"E17.bottom"),sQuery(id+"F11.wireOp",EDGE,"E17.top"),sQuery(id+"F11.wireOp",EDGE,"E17.left"),sQuery(id+"F11.wireOp",EDGE,"E17.right"),sQuery(id+"F11.wireOp",EDGE,"E18.filletArc"),sQuery(id+"F11.wireOp",EDGE,"E19.filletArc"),sQuery(id+"F11.wireOp",EDGE,"E20.filletArc"),sQuery(id+"F11.wireOp",EDGE,"E21.filletArc"),sQuery(id+"F11.wireOp",EDGE,"E22.0"),sQuery(id+"F11.wireOp",EDGE,"E22.1"),sQuery(id+"F11.wireOp",EDGE,"E22.2"),sQuery(id+"F11.wireOp",EDGE,"E22.3"),sQuery(id+"F11.wireOp",EDGE,"E22.4"),sQuery(id+"F11.wireOp",EDGE,"E22.5"),sQuery(id+"F11.wireOp",EDGE,"E22.6"),sQuery(id+"F11.wireOp",EDGE,"E22.7")])]});
            hole(context, id + "F18", {"style" : HoleStyle.C_BORE, "endStyle" : HoleEndStyle.THROUGH, "holeDiameter" : 5.1 * mm, "cBoreDiameter" : 9.8 * mm, "cBoreDepth" : 0 * mm, "majorDiameter" : 5 * mm, "isTappedThrough" : true, "tappedDepth" : 12 * mm, "tapClearance" : 3, "locations" : qUnion([Q0]), "scope" : qUnion([Q1])});
        }
        {
            var Q0;
            Q0=makeQuery(id+"F11.imprint","IMPRINT",FACE,{"disambiguationData":[TD([[makeQuery(id+"F11.imprint","IMPRINT",EDGE,{"derivedFrom":sQuery(id+"F11.wireOp",EDGE,"E17.bottom")}),-1.0]])]});
            var sketch = newSketch(context, id + "F19", { "sketchPlane" : qUnion([Q0])});
            skArc(sketch, "E39.0", {"start": v(116.85, 15) * mm, "mid": v(114.62, 20.37) * mm, "end": v(109.25, 22.6) * mm});
            skLineSegment(sketch, "E39.1", {"start": v(116.85, -15) * mm, "end": v(116.85, 15) * mm});
            skLineSegment(sketch, "E39.2", {"start": v(109.25, 22.6) * mm, "end": v(89.25, 22.6) * mm});
            skArc(sketch, "E39.3", {"start": v(109.25, -22.6) * mm, "mid": v(114.62, -20.37) * mm, "end": v(116.85, -15) * mm});
            skArc(sketch, "E39.4", {"start": v(89.25, 22.6) * mm, "mid": v(83.87, 20.37) * mm, "end": v(81.65, 15) * mm});
            skLineSegment(sketch, "E39.5", {"start": v(81.65, -15) * mm, "end": v(81.65, 15) * mm});
            skArc(sketch, "E39.6", {"start": v(81.65, -15) * mm, "mid": v(83.87, -20.37) * mm, "end": v(89.25, -22.6) * mm});
            skLineSegment(sketch, "E39.7", {"start": v(109.25, -22.6) * mm, "end": v(89.25, -22.6) * mm});
            skArc(sketch, "E40.0", {"start": v(109.25, -18.6) * mm, "mid": v(111.8, -17.55) * mm, "end": v(112.85, -15) * mm});
            skLineSegment(sketch, "E40.1", {"start": v(109.25, -18.6) * mm, "end": v(89.25, -18.6) * mm});
            skLineSegment(sketch, "E40.2", {"start": v(112.85, -15) * mm, "end": v(112.85, 15) * mm});
            skArc(sketch, "E40.3", {"start": v(85.65, -15) * mm, "mid": v(86.7, -17.55) * mm, "end": v(89.25, -18.6) * mm});
            skArc(sketch, "E40.4", {"start": v(112.85, 15) * mm, "mid": v(111.8, 17.55) * mm, "end": v(109.25, 18.6) * mm});
            skLineSegment(sketch, "E40.5", {"start": v(109.25, 18.6) * mm, "end": v(89.25, 18.6) * mm});
            skArc(sketch, "E40.6", {"start": v(89.25, 18.6) * mm, "mid": v(86.7, 17.55) * mm, "end": v(85.65, 15) * mm});
            skLineSegment(sketch, "E40.7", {"start": v(85.65, -15) * mm, "end": v(85.65, 15) * mm});
            skCircle(sketch, "E41", {"center": v(99.23, 0) * mm, "radius": 10.6 * mm});
            skCircle(sketch, "E42", {"center": v(99.23, 0) * mm, "radius": 11.9 * mm});
            skSolve(sketch);
        }
        {
            var Q0;
            Q0=qSketchRegion(id+"F19",true);
            var Q1;
            Q1=makeQuery(id+"F19.imprint","IMPRINT",FACE,{"disambiguationData":[TD([[makeQuery(id+"F19.imprint","IMPRINT",EDGE,{"derivedFrom":sQuery(id+"F19.wireOp",EDGE,"E40.0")}),1.0]])]});
            var Q2;
            Q2=makeQuery(id+"F19.imprint","IMPRINT",FACE,{"disambiguationData":[TD([[makeQuery(id+"F19.imprint","IMPRINT",EDGE,{"derivedFrom":sQuery(id+"F19.wireOp",EDGE,"E41")}),-1.0]])]});
            var Q3;
            Q3=makeQuery(id+"F19.imprint","IMPRINT",FACE,{"disambiguationData":[TD([[makeQuery(id+"F19.imprint","IMPRINT",EDGE,{"derivedFrom":sQuery(id+"F19.wireOp",EDGE,"E41")}),1.0]])]});
            extrude(context, id + "F20", {"entities" : qUnion([Q0, Q1, Q2, Q3]), "depth" : 28 * mm, "offsetDistance" : 25 * mm});
        }
        {
            var Q0;
            Q0=makeQuery(id+"F13.opExtrude","CAP_EDGE",EDGE,{"disambiguationData":[OSD([sQuery(id+"F11.wireOp",EDGE,"E17.bottom")])],"isStart":false});
            var Q1;
            Q1=makeQuery(id+"F9PtOEdPbCvG9N9_10.opChamfer","BLEND_EDGE",EDGE,{"blendedFrom":[makeQuery(id+"F13.opExtrude","CAP_EDGE",EDGE,{"disambiguationData":[OSD([sQuery(id+"F11.wireOp",EDGE,"E17.left")])],"isStart":false}),makeQuery(id+"F13.opExtrude","SWEPT_FACE",FACE,{"disambiguationData":[OSD([sQuery(id+"F11.wireOp",EDGE,"E19.filletArc")])]})],"blendedInto":[makeQuery(id+"F13.opExtrude","SWEPT_FACE",FACE,{"disambiguationData":[OSD([sQuery(id+"F11.wireOp",EDGE,"E19.filletArc")])]})]});
            var Q2;
            Q2=makeQuery(id+"F9PtOEdPbCvG9N9_10.opChamfer","BLEND_EDGE",EDGE,{"blendedFrom":[makeQuery(id+"F13.opExtrude","CAP_EDGE",EDGE,{"disambiguationData":[OSD([sQuery(id+"F11.wireOp",EDGE,"E17.right")])],"isStart":false}),makeQuery(id+"F13.opExtrude","SWEPT_FACE",FACE,{"disambiguationData":[OSD([sQuery(id+"F11.wireOp",EDGE,"E17.top")])]})],"blendedInto":[makeQuery(id+"F13.opExtrude","SWEPT_FACE",FACE,{"disambiguationData":[OSD([sQuery(id+"F11.wireOp",EDGE,"E17.top")])]})]});
            var Q3;
            Q3=makeQuery(id+"F13.opExtrude","CAP_FACE",FACE,{"disambiguationData":[OSD([sQuery(id+"F11.wireOp",EDGE,"E17.bottom"),sQuery(id+"F11.wireOp",EDGE,"E17.top"),sQuery(id+"F11.wireOp",EDGE,"E17.left"),sQuery(id+"F11.wireOp",EDGE,"E17.right"),sQuery(id+"F11.wireOp",EDGE,"E18.filletArc"),sQuery(id+"F11.wireOp",EDGE,"E19.filletArc"),sQuery(id+"F11.wireOp",EDGE,"E20.filletArc"),sQuery(id+"F11.wireOp",EDGE,"E21.filletArc")])],"isStart":false});
            chamfer(context, id + "F21", {"entities" : qUnion([Q0, Q1, Q2, Q3]), "width" : 2 * mm, "tangentPropagation" : true});
        }
        {
            var Q0;
            Q0=makeQuery(id+"F12.opExtrude","SWEPT_BODY",BODY,{"disambiguationData":[OSD([sQuery(id+"F11.wireOp",EDGE,"E17.bottom"),sQuery(id+"F11.wireOp",EDGE,"E17.top"),sQuery(id+"F11.wireOp",EDGE,"E17.left"),sQuery(id+"F11.wireOp",EDGE,"E17.right"),sQuery(id+"F11.wireOp",EDGE,"E18.filletArc"),sQuery(id+"F11.wireOp",EDGE,"E19.filletArc"),sQuery(id+"F11.wireOp",EDGE,"E20.filletArc"),sQuery(id+"F11.wireOp",EDGE,"E21.filletArc"),sQuery(id+"F11.wireOp",EDGE,"E22.0"),sQuery(id+"F11.wireOp",EDGE,"E22.1"),sQuery(id+"F11.wireOp",EDGE,"E22.2"),sQuery(id+"F11.wireOp",EDGE,"E22.3"),sQuery(id+"F11.wireOp",EDGE,"E22.4"),sQuery(id+"F11.wireOp",EDGE,"E22.5"),sQuery(id+"F11.wireOp",EDGE,"E22.6"),sQuery(id+"F11.wireOp",EDGE,"E22.7")])]});
            var Q1;
            Q1=makeQuery(id+"F13.opExtrude","SWEPT_BODY",BODY,{"disambiguationData":[OSD([sQuery(id+"F11.wireOp",EDGE,"E17.bottom"),sQuery(id+"F11.wireOp",EDGE,"E17.top"),sQuery(id+"F11.wireOp",EDGE,"E17.left"),sQuery(id+"F11.wireOp",EDGE,"E17.right"),sQuery(id+"F11.wireOp",EDGE,"E18.filletArc"),sQuery(id+"F11.wireOp",EDGE,"E19.filletArc"),sQuery(id+"F11.wireOp",EDGE,"E20.filletArc"),sQuery(id+"F11.wireOp",EDGE,"E21.filletArc")])]});
            booleanBodies(context, id + "F22", {"operationType" : BooleanOperationType.UNION, "tools" : qUnion([Q0, Q1])});
        }
        {
            var Q0;
            Q0=makeQuery(id+"F20.opExtrude","CAP_FACE",FACE,{"disambiguationData":[OSD([sQuery(id+"F19.wireOp",EDGE,"E39.0"),sQuery(id+"F19.wireOp",EDGE,"E39.1"),sQuery(id+"F19.wireOp",EDGE,"E39.2"),sQuery(id+"F19.wireOp",EDGE,"E39.3"),sQuery(id+"F19.wireOp",EDGE,"E39.4"),sQuery(id+"F19.wireOp",EDGE,"E39.5"),sQuery(id+"F19.wireOp",EDGE,"E39.6"),sQuery(id+"F19.wireOp",EDGE,"E39.7"),sQuery(id+"F19.wireOp",EDGE,"E41")])],"isStart":false});
            cPlane(context, id + "F23", {"entities" : qUnion([Q0]), "cplaneType" : CPlaneType.OFFSET, "offset" : 0 * mm, "width" : 150 * mm, "height" : 150 * mm});
        }
        {
            var Q0;
            Q0=qCreatedBy(id+"F23.planeOp",FACE);
            var sketch = newSketch(context, id + "F24", { "sketchPlane" : qUnion([Q0])});
            skPoint(sketch, "E43", {"position": v(98.96, 0) * mm});
            skSolve(sketch);
        }
        {
            var Q0;
            Q0=sQuery(id+"F24.wireOp",VERTEX,"E43");
            var Q1;
            Q1=makeQuery(id+"F20.opExtrude","SWEPT_BODY",BODY,{"disambiguationData":[OSD([sQuery(id+"F19.wireOp",EDGE,"E39.0"),sQuery(id+"F19.wireOp",EDGE,"E39.1"),sQuery(id+"F19.wireOp",EDGE,"E39.2"),sQuery(id+"F19.wireOp",EDGE,"E39.3"),sQuery(id+"F19.wireOp",EDGE,"E39.4"),sQuery(id+"F19.wireOp",EDGE,"E39.5"),sQuery(id+"F19.wireOp",EDGE,"E39.6"),sQuery(id+"F19.wireOp",EDGE,"E39.7"),sQuery(id+"F19.wireOp",EDGE,"E41")])]});
            hole(context, id + "F25", {"style" : HoleStyle.SIMPLE, "endStyle" : HoleEndStyle.BLIND, "holeDiameter" : 6 * mm, "majorDiameter" : 5 * mm, "holeDepth" : 25 * mm, "isTappedThrough" : true, "tappedDepth" : 12 * mm, "tapClearance" : 3, "locations" : qUnion([Q0]), "scope" : qUnion([Q1])});
        }
        {
            var Q0;
            Q0=makeQuery(id+"F11.imprint","IMPRINT",FACE,{"disambiguationData":[TD([[makeQuery(id+"F11.imprint","IMPRINT",EDGE,{"derivedFrom":sQuery(id+"F11.wireOp",EDGE,"E22.0")}),1.0]])]});
            extrude(context, id + "F26", {"entities" : qUnion([Q0]), "operationType" : NewBodyOperationType.REMOVE, "depth" : 10 * mm, "offsetDistance" : 25 * mm});
        }
        {
            var Q0;
            Q0=makeQuery(id+"F16.boolean.opBoolean","INTERSECT",EDGE,{"derivedFrom":[makeQuery(id+"F12.opExtrude","SWEPT_FACE",FACE,{"disambiguationData":[OSD([sQuery(id+"F11.wireOp",EDGE,"E17.bottom")])]}),makeQuery(id+"F16.opExtrude","CAP_FACE",FACE,{"disambiguationData":[OSD([sQuery(id+"F15.wireOp",EDGE,"E30"),sQuery(id+"F15.wireOp",EDGE,"E31"),sQuery(id+"F15.wireOp",EDGE,"E35"),sQuery(id+"F15.wireOp",EDGE,"E36"),sQuery(id+"F15.wireOp",EDGE,"E37")])],"isStart":true})]});
            var Q1;
            Q1=makeQuery(id+"F16.boolean.opBoolean","INTERSECT",EDGE,{"derivedFrom":[makeQuery(id+"F12.opExtrude","SWEPT_FACE",FACE,{"disambiguationData":[OSD([sQuery(id+"F11.wireOp",EDGE,"E17.bottom")])]}),makeQuery(id+"F16.opExtrude","CAP_FACE",FACE,{"disambiguationData":[OSD([sQuery(id+"F15.wireOp",EDGE,"E30"),sQuery(id+"F15.wireOp",EDGE,"E31"),sQuery(id+"F15.wireOp",EDGE,"E35"),sQuery(id+"F15.wireOp",EDGE,"E36"),sQuery(id+"F15.wireOp",EDGE,"E37")])],"isStart":false})]});
            chamfer(context, id + "F27", {"entities" : qUnion([Q0, Q1]), "width" : 4 * mm, "tangentPropagation" : true});
        }
        {
            var Q0;
            {var subQ0=sQuery(id+"F11.wireOp",EDGE,"E17.bottom");Q0=makeQuery(id+"F22.opBoolean","MERGE",FACE,{"derivedFrom":[makeQuery(id+"F12.opExtrude","SWEPT_FACE",FACE,{"disambiguationData":[OSD([subQ0])]}),makeQuery(id+"F13.opExtrude","SWEPT_FACE",FACE,{"disambiguationData":[OSD([subQ0])]})]});}
            cPlane(context, id + "F28", {"entities" : qUnion([Q0]), "cplaneType" : CPlaneType.OFFSET, "offset" : 0 * mm, "width" : 150 * mm, "height" : 150 * mm});
        }
        {
            var Q0;
            Q0=qCreatedBy(id+"F28.planeOp",FACE);
            var sketch = newSketch(context, id + "F29", { "sketchPlane" : qUnion([Q0])});
            skLineSegment(sketch, "E44", {"start": v(108.05, 0) * mm, "end": v(108.05, 64.93) * mm, "construction": true});
            skPoint(sketch, "E45", {"position": v(108.05, 31.3) * mm});
            skCircle(sketch, "E46", {"center": v(108.05, 31.3) * mm, "radius": 4 * mm});
            skSolve(sketch);
        }
        {
            var Q0;
            Q0=sQuery(id+"F29.wireOp",VERTEX,"E45");
            var Q1;
            Q1=makeQuery(id+"F12.opExtrude","SWEPT_BODY",BODY,{"disambiguationData":[OSD([sQuery(id+"F11.wireOp",EDGE,"E17.bottom"),sQuery(id+"F11.wireOp",EDGE,"E17.top"),sQuery(id+"F11.wireOp",EDGE,"E17.left"),sQuery(id+"F11.wireOp",EDGE,"E17.right"),sQuery(id+"F11.wireOp",EDGE,"E18.filletArc"),sQuery(id+"F11.wireOp",EDGE,"E19.filletArc"),sQuery(id+"F11.wireOp",EDGE,"E20.filletArc"),sQuery(id+"F11.wireOp",EDGE,"E21.filletArc"),sQuery(id+"F11.wireOp",EDGE,"E28.0"),sQuery(id+"F11.wireOp",EDGE,"E28.1"),sQuery(id+"F11.wireOp",EDGE,"E28.2"),sQuery(id+"F11.wireOp",EDGE,"E28.3"),sQuery(id+"F11.wireOp",EDGE,"E28.4"),sQuery(id+"F11.wireOp",EDGE,"E28.5"),sQuery(id+"F11.wireOp",EDGE,"E28.6"),sQuery(id+"F11.wireOp",EDGE,"E28.7")])]});
            hole(context, id + "F30", {"style" : HoleStyle.SIMPLE, "endStyle" : HoleEndStyle.BLIND, "holeDiameter" : 8 * mm, "majorDiameter" : 5 * mm, "holeDepth" : 6 * mm, "isTappedThrough" : true, "tappedDepth" : 12 * mm, "tapClearance" : 3, "locations" : qUnion([Q0]), "scope" : qUnion([Q1])});
        }
        {
            var Q0;
            Q0=makeQuery(id+"F19.imprint","IMPRINT",FACE,{"disambiguationData":[TD([[makeQuery(id+"F19.imprint","IMPRINT",EDGE,{"derivedFrom":sQuery(id+"F19.wireOp",EDGE,"E41")}),1.0]])]});
            extrude(context, id + "F31", {"entities" : qUnion([Q0]), "operationType" : NewBodyOperationType.REMOVE, "depth" : 8 * mm, "offsetDistance" : 25 * mm});
        }
        {
            var Q0;
            Q0=makeQuery(id+"F20.opExtrude","CAP_EDGE",EDGE,{"disambiguationData":[OSD([sQuery(id+"F19.wireOp",EDGE,"E39.5")])],"isStart":false});
            chamfer(context, id + "F32", {"entities" : qUnion([Q0]), "width" : 2 * mm, "tangentPropagation" : true});
        }
        {
            var Q0;
            Q0=makeQuery(id+"F20.opExtrude","SWEPT_BODY",BODY,{"disambiguationData":[OSD([sQuery(id+"F19.wireOp",EDGE,"E39.0"),sQuery(id+"F19.wireOp",EDGE,"E39.1"),sQuery(id+"F19.wireOp",EDGE,"E39.2"),sQuery(id+"F19.wireOp",EDGE,"E39.3"),sQuery(id+"F19.wireOp",EDGE,"E39.4"),sQuery(id+"F19.wireOp",EDGE,"E39.5"),sQuery(id+"F19.wireOp",EDGE,"E39.6"),sQuery(id+"F19.wireOp",EDGE,"E39.7")])]});
            var Q1;
            Q1=sQuery(id+"F29.wireOp",EDGE,"E44");
            transform(context, id + "F33", {"entities" : qUnion([Q0]), "transformType" : TransformType.TRANSLATION_DISTANCE, "transformDirection" : qUnion([Q1]), "distance" : 18 * mm, "oppositeDirection" : true, "makeCopy" : false});
        }
    });
